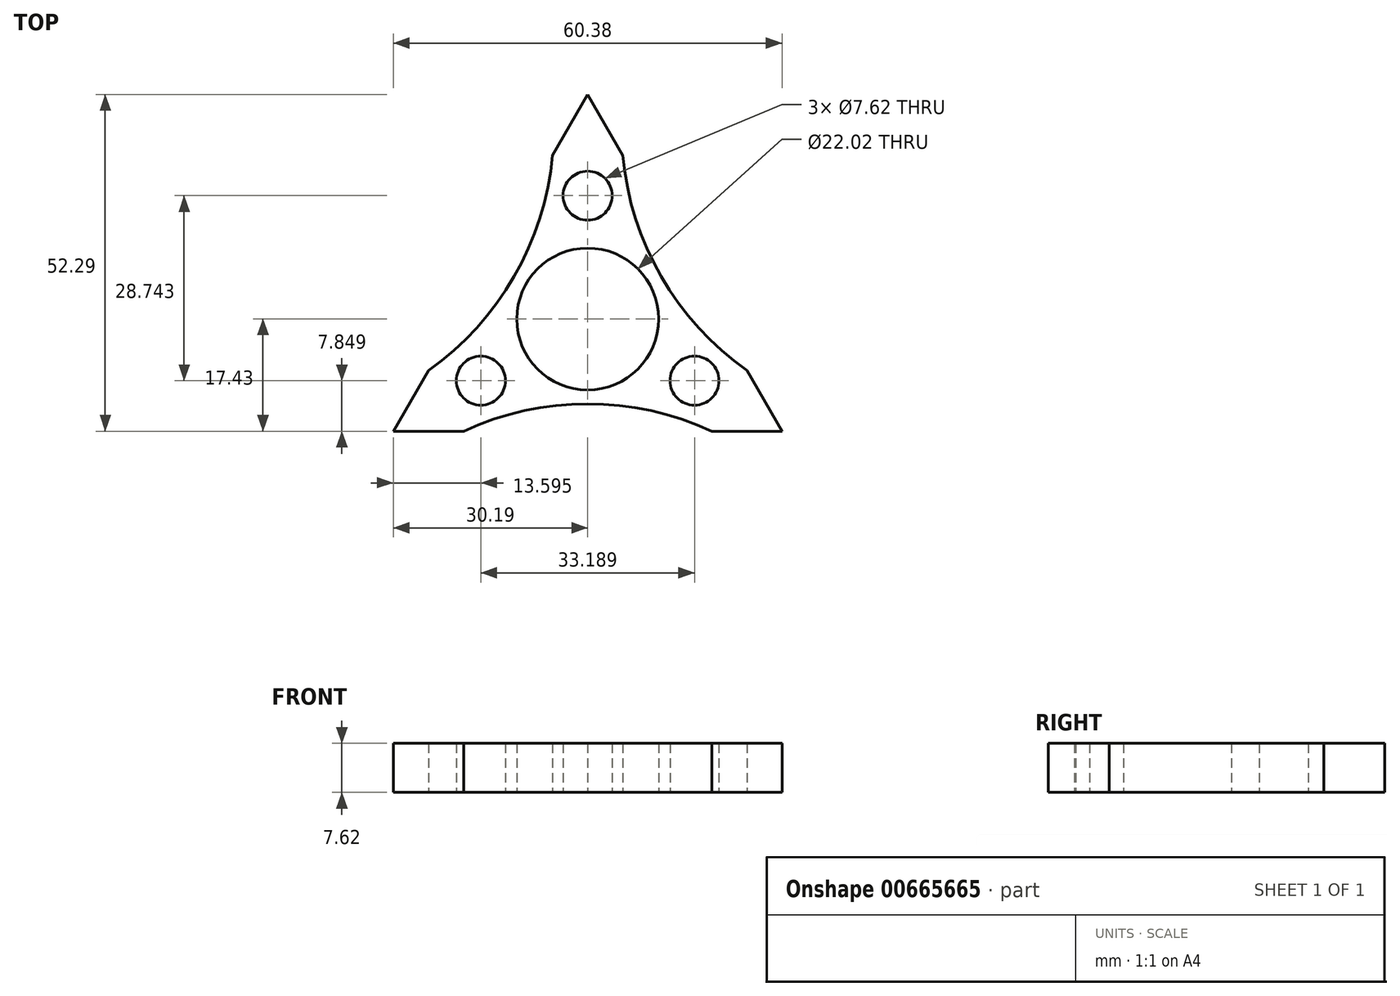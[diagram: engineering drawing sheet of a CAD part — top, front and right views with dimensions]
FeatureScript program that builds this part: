
annotation { "Feature Type Name" : "Feature", "Feature Type Description" : "" }
export const myFeature = defineFeature(function(context is Context, id is Id, definition is map)
    precondition{}
    {
        {
            var Q0;
            Q0=qCreatedBy(makeId("Top.planeOp"),FACE);
            var sketch = newSketch(context, id + "F0", { "sketchPlane" : qUnion([Q0])});
            skCircle(sketch, "E0", {"center": v(0, 0) * mm, "radius": 11.01 * mm});
            skLineSegment(sketch, "E1.0", {"start": v(0, 34.86) * mm, "end": v(5.46, 25.4) * mm});
            skLineSegment(sketch, "E1.2", {"start": v(-5.46, 25.4) * mm, "end": v(0, 34.86) * mm});
            skPoint(sketch, "E1.0.midPoint", {"position": v(2.73, 30.13) * mm});
            skLineSegment(sketch, "E2.1.1", {"start": v(-30.19, -17.43) * mm, "end": v(-24.73, -7.97) * mm});
            skLineSegment(sketch, "E2.1.2", {"start": v(-19.27, -17.43) * mm, "end": v(-30.19, -17.43) * mm});
            skLineSegment(sketch, "E2.2.1", {"start": v(30.19, -17.43) * mm, "end": v(19.27, -17.43) * mm});
            skLineSegment(sketch, "E2.2.2", {"start": v(24.73, -7.97) * mm, "end": v(30.19, -17.43) * mm});
            skPoint(sketch, "E3.orphan", {"position": v(-11.75, 8.9) * mm});
            skPoint(sketch, "E4.trimOffspring.start.orphan", {"position": v(11.75, 8.9) * mm});
            skPoint(sketch, "E5.orphan", {"position": v(1.83, -14.62) * mm});
            skArc(sketch, "E6", {"start": v(5.46, 25.4) * mm, "mid": v(11.42, 6.6) * mm, "end": v(24.73, -7.97) * mm});
            skArc(sketch, "E7.1.0", {"start": v(-24.73, -7.97) * mm, "mid": v(-11.42, 6.6) * mm, "end": v(-5.46, 25.4) * mm});
            skArc(sketch, "E7.2.0", {"start": v(19.27, -17.43) * mm, "mid": v(0, -13.19) * mm, "end": v(-19.27, -17.43) * mm});
            skCircle(sketch, "E8", {"center": v(0, 19.16) * mm, "radius": 3.81 * mm});
            skCircle(sketch, "E9.1.0", {"center": v(-16.6, -9.58) * mm, "radius": 3.81 * mm});
            skCircle(sketch, "E9.2.0", {"center": v(16.6, -9.58) * mm, "radius": 3.81 * mm});
            skSolve(sketch);
        }
        {
            var Q0;
            Q0 = qSketchRegion(id + "F0", true);
            extrude(context, id + "F1", {"entities" : qUnion([Q0]), "depth" : 7.62 * mm, "offsetDistance" : 25.4 * mm});
        }
    });
